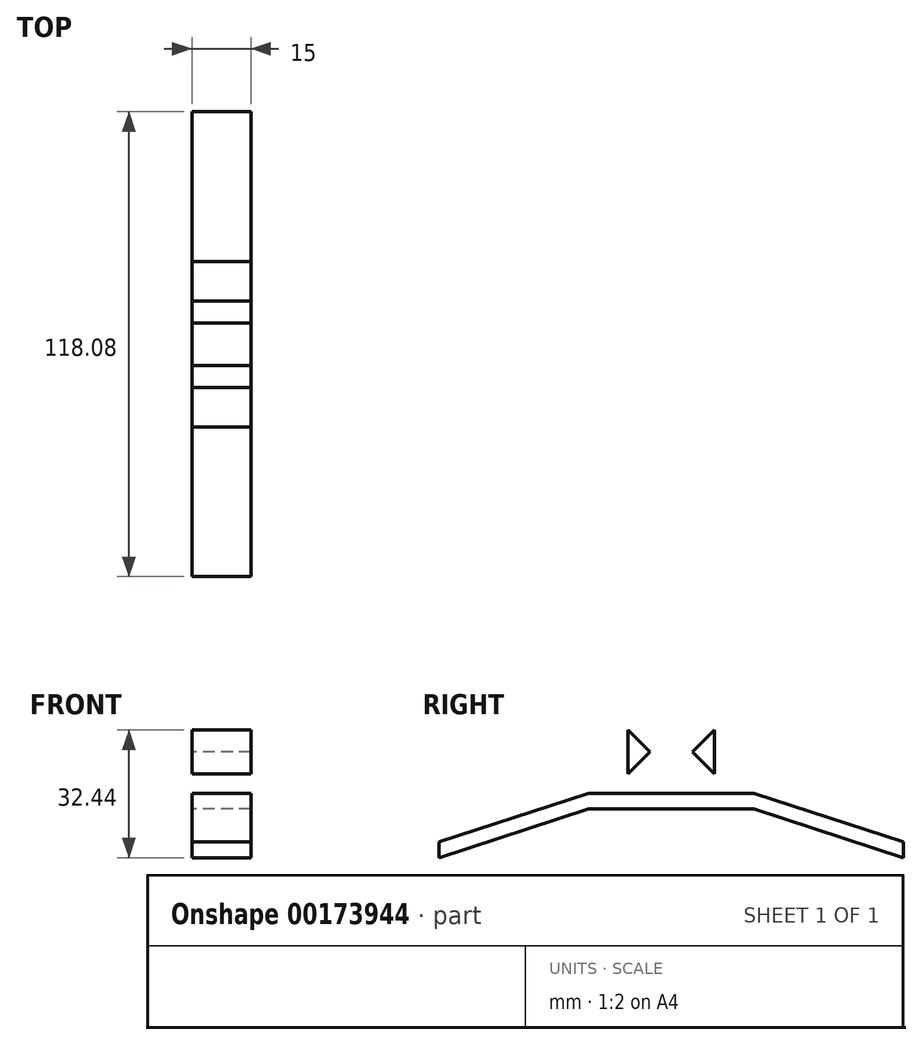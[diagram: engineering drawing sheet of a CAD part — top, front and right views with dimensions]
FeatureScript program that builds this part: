
annotation { "Feature Type Name" : "Feature", "Feature Type Description" : "" }
export const myFeature = defineFeature(function(context is Context, id is Id, definition is map)
    precondition{}
    {
        {
            var Q0;
            Q0=qCreatedBy(makeId("Right.planeOp"),FACE);
            var sketch = newSketch(context, id + "F0", { "sketchPlane" : qUnion([Q0])});
            skLineSegment(sketch, "E0.bottom", {"start": v(-21, 0) * mm, "end": v(21, 0) * mm});
            skLineSegment(sketch, "E0.top", {"start": v(-21, 4) * mm, "end": v(21, 4) * mm});
            skLineSegment(sketch, "E0.left", {"start": v(-21, 0) * mm, "end": v(-21, 4) * mm});
            skLineSegment(sketch, "E0.right", {"start": v(21, 0) * mm, "end": v(21, 4) * mm});
            skLineSegment(sketch, "E1.bottom", {"start": v(21, 4) * mm, "end": v(11, 4) * mm});
            skLineSegment(sketch, "E1.top", {"start": v(21, 25) * mm, "end": v(11, 25) * mm});
            skLineSegment(sketch, "E1.left", {"start": v(21, 4) * mm, "end": v(21, 25) * mm});
            skLineSegment(sketch, "E1.right", {"start": v(11, 4) * mm, "end": v(11, 25) * mm});
            skLineSegment(sketch, "E2", {"start": v(0, 0) * mm, "end": v(0, 12.87) * mm});
            skLineSegment(sketch, "E3.MirrorCS", {"start": v(-11, 4) * mm, "end": v(-11, 25) * mm});
            skLineSegment(sketch, "E4.MirrorCS", {"start": v(-21, 25) * mm, "end": v(-11, 25) * mm});
            skLineSegment(sketch, "E5.MirrorCS", {"start": v(-21, 4) * mm, "end": v(-21, 25) * mm});
            skLineSegment(sketch, "E6.MirrorCS", {"start": v(-21, 4) * mm, "end": v(-11, 4) * mm});
            skLineSegment(sketch, "E7", {"start": v(11, 20.08) * mm, "end": v(5.42, 14.5) * mm});
            skPoint(sketch, "E7.endSnap0", {"position": v(11, 14.5) * mm});
            skLineSegment(sketch, "E8", {"start": v(5.42, 14.5) * mm, "end": v(11, 8.92) * mm});
            skLineSegment(sketch, "E9.MirrorCS", {"start": v(-5.42, 14.5) * mm, "end": v(-11, 8.92) * mm});
            skLineSegment(sketch, "E10.MirrorCS", {"start": v(-11, 20.08) * mm, "end": v(-5.42, 14.5) * mm});
            skLineSegment(sketch, "E11", {"start": v(-13, 25) * mm, "end": v(-21, 4) * mm});
            skLineSegment(sketch, "E12", {"start": v(13, 25) * mm, "end": v(21, 4) * mm});
            skLineSegment(sketch, "E13", {"start": v(21, 0) * mm, "end": v(59.04, -12.36) * mm});
            skLineSegment(sketch, "E14", {"start": v(59.04, -12.36) * mm, "end": v(59.04, -8.36) * mm});
            skLineSegment(sketch, "E15", {"start": v(59.04, -8.36) * mm, "end": v(21, 4) * mm});
            skLineSegment(sketch, "E16", {"start": v(-21, 0) * mm, "end": v(-59.04, -12.36) * mm});
            skLineSegment(sketch, "E17", {"start": v(-59.04, -12.36) * mm, "end": v(-59.04, -8.36) * mm});
            skLineSegment(sketch, "E18", {"start": v(-59.04, -8.36) * mm, "end": v(-21, 4) * mm});
            skSolve(sketch);
        }
        {
            var Q0;
            {var subQ0=sQuery(id+"F0.wireOp",EDGE,"E7");Q0=makeQuery(id+"F0.imprint","IMPRINT",FACE,{"disambiguationData":[TD([[makeQuery(id+"F0.imprint","IMPRINT",EDGE,{"derivedFrom":subQ0}),1.0]])]});}
            var Q1;
            {var subQ0=sQuery(id+"F0.wireOp",EDGE,"E9.MirrorCS");Q1=makeQuery(id+"F0.imprint","IMPRINT",FACE,{"disambiguationData":[TD([[makeQuery(id+"F0.imprint","IMPRINT",EDGE,{"derivedFrom":subQ0}),-1.0]])]});}
            var Q2;
            {var subQ5=sQuery(id+"F0.wireOp",EDGE,"E0.left");Q2=makeQuery(id+"F0.imprint","IMPRINT",FACE,{"disambiguationData":[TD([[makeQuery(id+"F0.imprint","IMPRINT",EDGE,{"derivedFrom":subQ5}),-1.0]])]});}
            var Q3;
            {var subQ1=sQuery(id+"F0.wireOp",EDGE,"E0.right");Q3=makeQuery(id+"F0.imprint","IMPRINT",FACE,{"disambiguationData":[TD([[makeQuery(id+"F0.imprint","IMPRINT",EDGE,{"derivedFrom":subQ1}),1.0]])]});}
            var Q4;
            {var subQ4=sQuery(id+"F0.wireOp",EDGE,"E1.bottom");Q4=makeQuery(id+"F0.imprint","IMPRINT",FACE,{"disambiguationData":[TD([[makeQuery(id+"F0.imprint","IMPRINT",EDGE,{"derivedFrom":subQ4}),-1.0]])]});}
            var Q5;
            {var subQ0=sQuery(id+"F0.wireOp",EDGE,"E6.MirrorCS");Q5=makeQuery(id+"F0.imprint","IMPRINT",FACE,{"disambiguationData":[TD([[makeQuery(id+"F0.imprint","IMPRINT",EDGE,{"derivedFrom":subQ0}),1.0]])]});}
            var Q6;
            Q6=makeQuery(id+"F0.imprint","IMPRINT",FACE,{"disambiguationData":[TD([[makeQuery(id+"F0.imprint","IMPRINT",EDGE,{"derivedFrom":sQuery(id+"F0.wireOp",EDGE,"XS8kGLH5-8osO-NL46-Pnvk-7tKazz9557V3.bottom")}),-1.0]])]});
            var Q7;
            {var subQ0=sQuery(id+"F0.wireOp",EDGE,"E6.MirrorCS");Q7=makeQuery(id+"F0.imprint","IMPRINT",FACE,{"disambiguationData":[TD([[makeQuery(id+"F0.imprint","IMPRINT",EDGE,{"derivedFrom":subQ0}),-1.0]])]});}
            var Q8;
            Q8=makeQuery(id+"F0.imprint","IMPRINT",FACE,{"disambiguationData":[TD([[makeQuery(id+"F0.imprint","IMPRINT",EDGE,{"derivedFrom":sQuery(id+"F0.wireOp",EDGE,"C1Eb2igc-bLC3-ctj1-j9Kr-RpPUlgWRj01e.bottom")}),1.0]])]});
            var Q9;
            {var subQ0=sQuery(id+"F0.wireOp",EDGE,"E1.bottom");Q9=makeQuery(id+"F0.imprint","IMPRINT",FACE,{"disambiguationData":[TD([[makeQuery(id+"F0.imprint","IMPRINT",EDGE,{"derivedFrom":subQ0}),1.0]])]});}
            var Q10;
            Q10=makeQuery(id+"F0.imprint","IMPRINT",FACE,{"disambiguationData":[TD([[makeQuery(id+"F0.imprint","IMPRINT",EDGE,{"derivedFrom":sQuery(id+"F0.wireOp",EDGE,"E0.right")}),-1.0]])]});
            var Q11;
            Q11=makeQuery(id+"F0.imprint","IMPRINT",FACE,{"disambiguationData":[TD([[makeQuery(id+"F0.imprint","IMPRINT",EDGE,{"derivedFrom":sQuery(id+"F0.wireOp",EDGE,"E0.left")}),1.0]])]});
            extrude(context, id + "F1", {"entities" : qUnion([Q0, Q1, Q2, Q3, Q4, Q5, Q6, Q7, Q8, Q9, Q10, Q11]), "offsetDistance" : 25 * mm, "depth" : 15 * mm});
        }
    });
